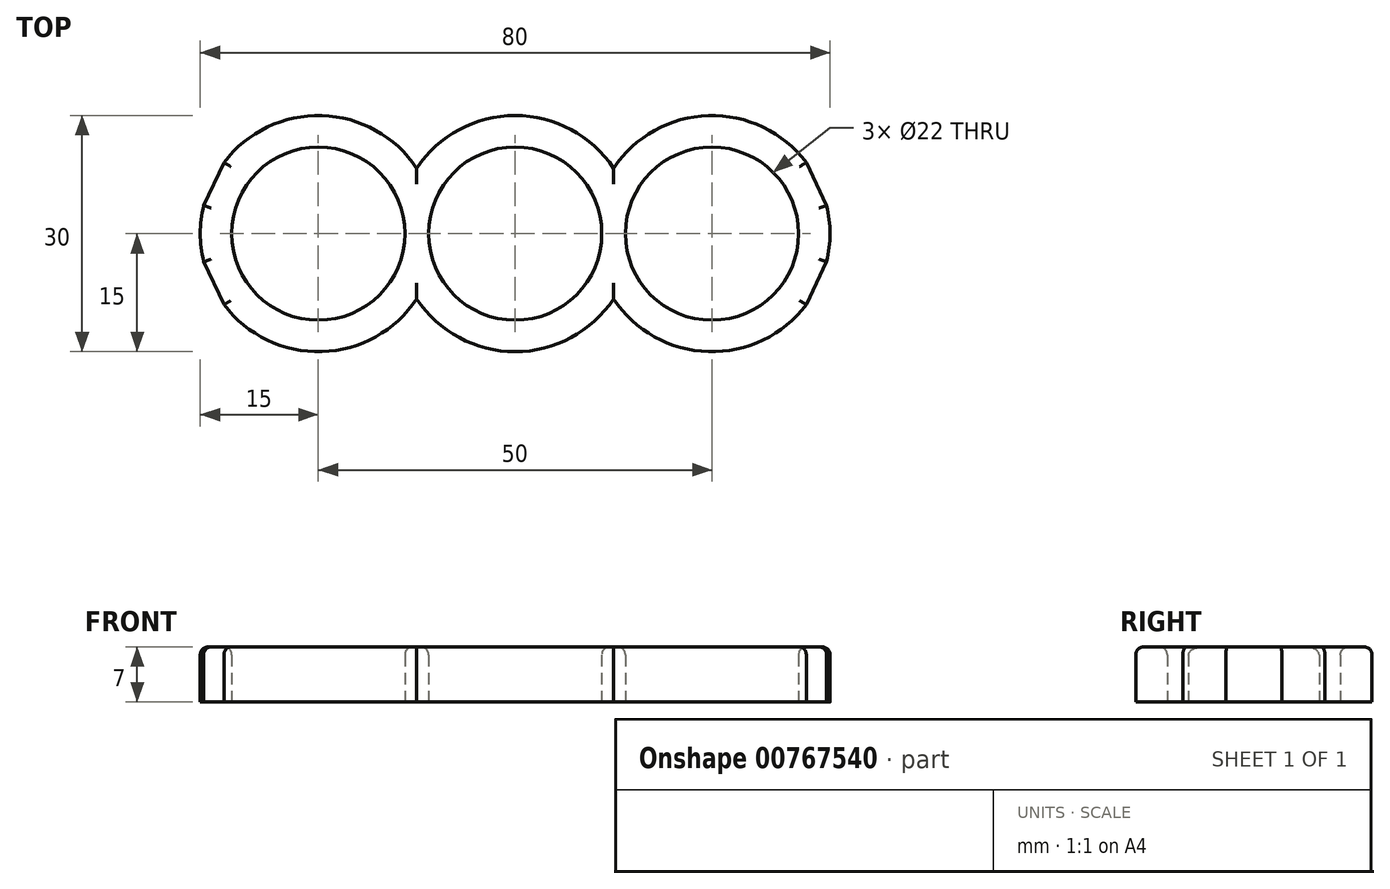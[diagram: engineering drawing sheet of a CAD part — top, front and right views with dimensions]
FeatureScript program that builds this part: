
annotation { "Feature Type Name" : "Feature", "Feature Type Description" : "" }
export const myFeature = defineFeature(function(context is Context, id is Id, definition is map)
    precondition{}
    {
        {
            var Q0;
            Q0=qCreatedBy(makeId("Top.planeOp"),FACE);
            var sketch = newSketch(context, id + "F0", { "sketchPlane" : qUnion([Q0])});
            skArc(sketch, "E0", {"start": v(0, 11) * mm, "mid": v(-11, 0) * mm, "end": v(0, -11) * mm});
            skArc(sketch, "E1", {"start": v(-12.5, -8.3) * mm, "mid": v(-7.1, -13.22) * mm, "end": v(0, -15) * mm});
            skCircle(sketch, "E2", {"center": v(-25, 0) * mm, "radius": 11 * mm});
            skArc(sketch, "E3.trimOffspring", {"start": v(-12.5, 8.3) * mm, "mid": v(-24.55, 15) * mm, "end": v(-36.98, 9.03) * mm});
            skArc(sketch, "E4.trimOffspring", {"start": v(0, 15) * mm, "mid": v(-7.1, 13.22) * mm, "end": v(-12.5, 8.3) * mm});
            skArc(sketch, "E5.MirrorCS", {"start": v(12.5, 8.3) * mm, "mid": v(24.55, 15) * mm, "end": v(36.98, 9.03) * mm});
            skCircle(sketch, "E6.MirrorC", {"center": v(25, 0) * mm, "radius": 11 * mm});
            skArc(sketch, "E7.MirrorCS", {"start": v(0, 15) * mm, "mid": v(7.1, 13.22) * mm, "end": v(12.5, 8.3) * mm});
            skArc(sketch, "E8.MirrorCS", {"start": v(12.5, -8.3) * mm, "mid": v(7.1, -13.22) * mm, "end": v(0, -15) * mm});
            skArc(sketch, "E9.MirrorCS", {"start": v(0, 11) * mm, "mid": v(11, 0) * mm, "end": v(0, -11) * mm});
            skArc(sketch, "E10.trimOffspring", {"start": v(-36.98, -9.03) * mm, "mid": v(-24.55, -15) * mm, "end": v(-12.5, -8.3) * mm});
            skArc(sketch, "E11.trimOffspring", {"start": v(39.57, 3.58) * mm, "mid": v(40, 0) * mm, "end": v(39.57, -3.58) * mm});
            skArc(sketch, "E12.trimOffspring", {"start": v(36.98, -9.03) * mm, "mid": v(24.55, -15) * mm, "end": v(12.5, -8.3) * mm});
            skArc(sketch, "E13.trimOffspring", {"start": v(-39.57, 3.58) * mm, "mid": v(-40, 0) * mm, "end": v(-39.57, -3.58) * mm});
            skFitSpline(sketch, "E14", {"points": [v(-36.98, 9.03) * mm, v(-39.57, 3.58) * mm], "startDerivative": vector(-2.59, -5.45) * mm, "endDerivative": vector(-2.59, -5.45) * mm});
            skFitSpline(sketch, "E15", {"points": [v(-39.57, -3.58) * mm, v(-36.98, -9.03) * mm], "startDerivative": vector(2.59, -5.45) * mm, "endDerivative": vector(2.59, -5.45) * mm});
            skFitSpline(sketch, "E16", {"points": [v(36.98, 9.03) * mm, v(39.57, 3.58) * mm], "startDerivative": vector(2.59, -5.45) * mm, "endDerivative": vector(2.59, -5.45) * mm});
            skFitSpline(sketch, "E17", {"points": [v(39.57, -3.58) * mm, v(36.98, -9.03) * mm], "startDerivative": vector(-2.59, -5.45) * mm, "endDerivative": vector(-2.59, -5.45) * mm});
            skSolve(sketch);
        }
        {
            var Q0;
            Q0=qSketchRegion(id+"F0",true);
            extrude(context, id + "F1", {"entities" : qUnion([Q0]), "depth" : 7 * mm, "offsetDistance" : 25 * mm});
        }
        {
            var Q0;
            Q0=makeQuery(id+"F1.opExtrude","CAP_EDGE",EDGE,{"disambiguationData":[OSD([sQuery(id+"F0.wireOp",EDGE,"E2")])],"isStart":false});
            var Q1;
            Q1=makeQuery(id+"F1.opExtrude","CAP_FACE",FACE,{"disambiguationData":[OSD([sQuery(id+"F0.wireOp",EDGE,"E0"),sQuery(id+"F0.wireOp",EDGE,"E1"),sQuery(id+"F0.wireOp",EDGE,"E2"),sQuery(id+"F0.wireOp",EDGE,"E3.trimOffspring"),sQuery(id+"F0.wireOp",EDGE,"E4.trimOffspring"),sQuery(id+"F0.wireOp",EDGE,"E5.MirrorCS"),sQuery(id+"F0.wireOp",EDGE,"E6.MirrorC"),sQuery(id+"F0.wireOp",EDGE,"E8.MirrorCS"),sQuery(id+"F0.wireOp",EDGE,"E9.MirrorCS"),sQuery(id+"F0.wireOp",EDGE,"E7.MirrorCS")])],"isStart":false});
            fillet(context, id + "F2", {"entities" : qUnion([Q0, Q1]), "radius" : 1 * mm, "tangentPropagation" : true, "allowEdgeOverflow" : false});
        }
    });
